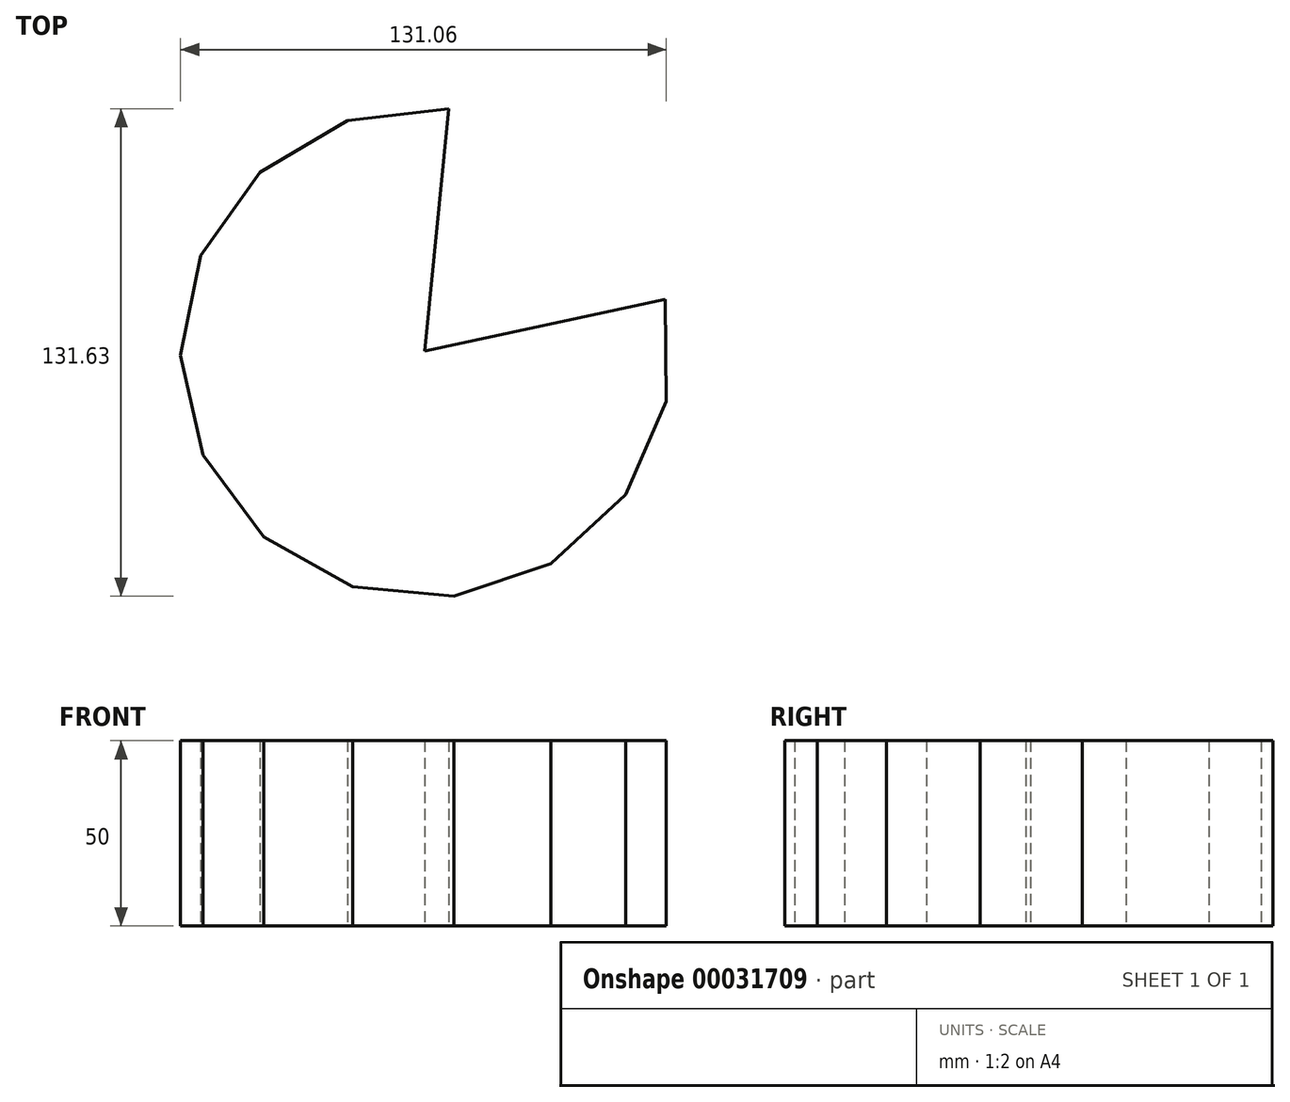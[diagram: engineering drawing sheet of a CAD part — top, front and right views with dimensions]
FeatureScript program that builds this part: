
annotation { "Feature Type Name" : "Feature", "Feature Type Description" : "" }
export const myFeature = defineFeature(function(context is Context, id is Id, definition is map)
    precondition{}
    {
        {
            var Q0;
            Q0=qCreatedBy(makeId("Top.planeOp"),FACE);
            var sketch = newSketch(context, id + "F0", { "sketchPlane" : qUnion([Q0])});
            skCircle(sketch, "E0.cCircle", {"center": v(0.31, -0.47) * mm, "radius": 64.74 * mm, "construction": true});
            skLineSegment(sketch, "E0.0", {"start": v(-20.81, 62.25) * mm, "end": v(6.52, 65.42) * mm});
            skLineSegment(sketch, "E0.1", {"start": v(6.52, 65.42) * mm, "end": v(32.79, 57.2) * mm});
            skLineSegment(sketch, "E0.2", {"start": v(32.79, 57.2) * mm, "end": v(53.43, 39) * mm});
            skLineSegment(sketch, "E0.3", {"start": v(53.43, 39) * mm, "end": v(64.9, 13.99) * mm});
            skLineSegment(sketch, "E0.4", {"start": v(64.9, 13.99) * mm, "end": v(65.19, -13.53) * mm});
            skLineSegment(sketch, "E0.5", {"start": v(65.19, -13.53) * mm, "end": v(54.27, -38.8) * mm});
            skLineSegment(sketch, "E0.6", {"start": v(54.27, -38.8) * mm, "end": v(34.01, -57.42) * mm});
            skLineSegment(sketch, "E0.7", {"start": v(34.01, -57.42) * mm, "end": v(7.93, -66.2) * mm});
            skLineSegment(sketch, "E0.8", {"start": v(7.93, -66.2) * mm, "end": v(-19.47, -63.62) * mm});
            skLineSegment(sketch, "E0.9", {"start": v(-19.47, -63.62) * mm, "end": v(-43.44, -50.12) * mm});
            skLineSegment(sketch, "E0.10", {"start": v(-43.44, -50.12) * mm, "end": v(-59.86, -28.03) * mm});
            skLineSegment(sketch, "E0.11", {"start": v(-59.86, -28.03) * mm, "end": v(-65.87, -1.17) * mm});
            skLineSegment(sketch, "E0.12", {"start": v(-65.87, -1.17) * mm, "end": v(-60.43, 25.8) * mm});
            skLineSegment(sketch, "E0.13", {"start": v(-60.43, 25.8) * mm, "end": v(-44.5, 48.24) * mm});
            skLineSegment(sketch, "E0.14", {"start": v(-44.5, 48.24) * mm, "end": v(-20.81, 62.25) * mm});
            skPoint(sketch, "E0.0.midPoint", {"position": v(-7.14, 63.84) * mm});
            skSolve(sketch);
        }
        {
            var Q0;
            Q0=makeQuery(id+"F0.imprint","IMPRINT",FACE,{"disambiguationData":[TD([[makeQuery(id+"F0.imprint","IMPRINT",EDGE,{"derivedFrom":sQuery(id+"F0.wireOp",EDGE,"E0.0")}),-1.0]])]});
            extrude(context, id + "F1", {"entities" : qUnion([Q0]), "depth" : 50 * mm});
        }
        {
            var Q0;
            Q0=makeQuery(id+"F1.opExtrude","CAP_FACE",FACE,{"disambiguationData":[OSD([sQuery(id+"F0.wireOp",EDGE,"E0.0"),sQuery(id+"F0.wireOp",EDGE,"E0.1"),sQuery(id+"F0.wireOp",EDGE,"E0.2"),sQuery(id+"F0.wireOp",EDGE,"E0.3"),sQuery(id+"F0.wireOp",EDGE,"E0.4"),sQuery(id+"F0.wireOp",EDGE,"E0.5"),sQuery(id+"F0.wireOp",EDGE,"E0.6"),sQuery(id+"F0.wireOp",EDGE,"E0.7"),sQuery(id+"F0.wireOp",EDGE,"E0.8"),sQuery(id+"F0.wireOp",EDGE,"E0.9"),sQuery(id+"F0.wireOp",EDGE,"E0.10"),sQuery(id+"F0.wireOp",EDGE,"E0.11"),sQuery(id+"F0.wireOp",EDGE,"E0.12"),sQuery(id+"F0.wireOp",EDGE,"E0.13"),sQuery(id+"F0.wireOp",EDGE,"E0.14")])],"isStart":true});
            var sketch = newSketch(context, id + "F2", { "sketchPlane" : qUnion([Q0])});
            skLineSegment(sketch, "E1", {"start": v(0, 0) * mm, "end": v(6.52, -65.42) * mm});
            skLineSegment(sketch, "E2", {"start": v(6.52, -65.42) * mm, "end": v(32.79, -57.2) * mm});
            skLineSegment(sketch, "E3", {"start": v(32.79, -57.2) * mm, "end": v(53.43, -39) * mm});
            skLineSegment(sketch, "E4", {"start": v(53.43, -39) * mm, "end": v(64.9, -13.99) * mm});
            skLineSegment(sketch, "E5", {"start": v(64.9, -13.99) * mm, "end": v(0, 0) * mm});
            skSolve(sketch);
        }
        {
            var Q0;
            Q0 = qSketchRegion(id + "F2", true);
            extrude(context, id + "F3", {"entities" : qUnion([Q0]), "operationType" : NewBodyOperationType.REMOVE, "oppositeDirection" : true, "depth" : 55 * mm});
        }
    });
